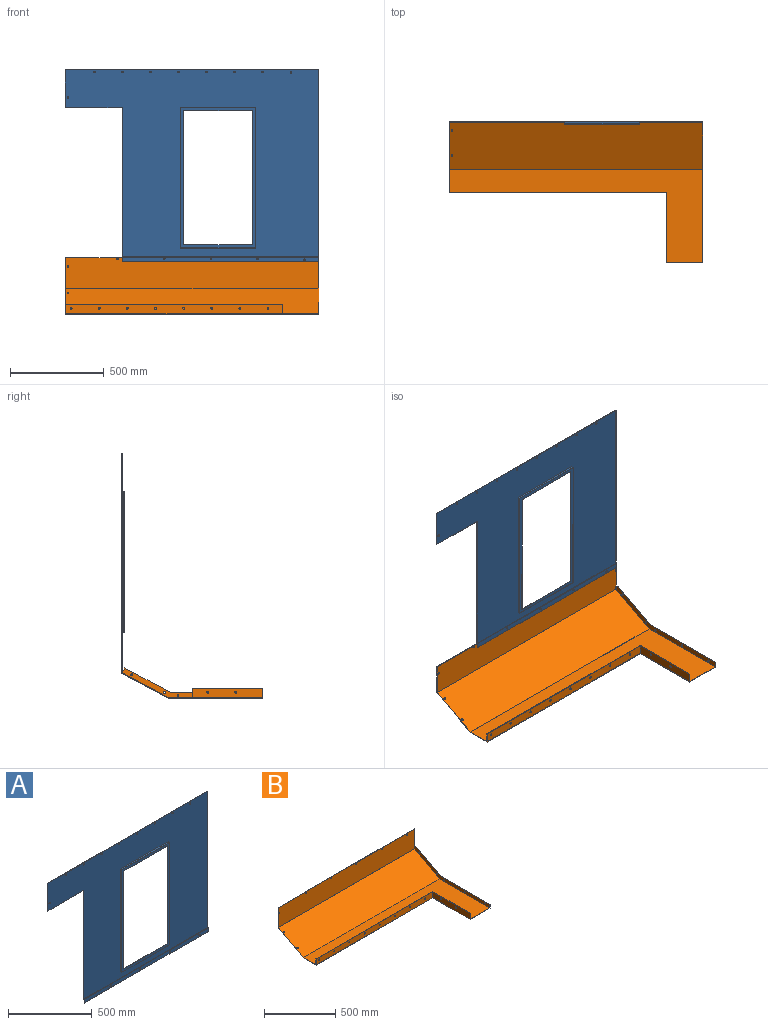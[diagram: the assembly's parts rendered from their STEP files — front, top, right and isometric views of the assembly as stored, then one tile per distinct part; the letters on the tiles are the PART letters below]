
ASSEMBLY  parts=2 mates=1
PART A: 66 faces, bbox 1352x14x1025.5 mm
  f0: plane 368x2mm, normal (0,0,-1), area 736mm2, adj f1,f2,f3,f4
  f1: plane 747.9x400mm, normal (0,1,0), area 35708.8mm2, adj f0,f2,f4,f5,f6,f7,f8,f9
  f2: plane 715.9x2mm, normal (-1,0,0), area 1431.8mm2, adj f0,f1,f3,f9
  f3: plane 751.9x404mm, normal (0,-1,0), area 40316.4mm2, adj f0,f2,f4,f9,f10,f11,f12,f13
  f4: plane 715.9x2mm, normal (1,0,0), area 1431.8mm2, adj f0,f1,f3,f9
  f5: plane 747.9x12mm, normal (-1,0,0), area 8974.8mm2, adj f1,f6,f8,f56
  f6: plane 400x12mm, normal (0,0,-1), area 4800mm2, adj f1,f5,f7,f56
  f7: plane 747.9x12mm, normal (1,0,0), area 8974.8mm2, adj f1,f6,f8,f56
  f8: plane 400x12mm, normal (0,0,1), area 4800mm2, adj f1,f5,f7,f56
  f9: plane 368x2mm, normal (0,0,1), area 736mm2, adj f1,f2,f3,f4
  f10: plane 751.9x12mm, normal (1,0,0), area 9022.8mm2, adj f3,f11,f13,f14
  f11: plane 404x12mm, normal (0,0,1), area 4848mm2, adj f3,f10,f12,f14
  f12: plane 751.9x12mm, normal (-1,0,0), area 9022.8mm2, adj f3,f11,f13,f14
  f13: plane 404x12mm, normal (0,0,-1), area 4848mm2, adj f3,f10,f12,f14
  f14: plane 1352x998.5mm, normal (0,-1,0), area 803361.6mm2, adj f10,f11,f12,f13,f15,f16,f17,f18
  f15: plane 1352x2mm, normal (0,0,1), area 2704mm2, adj f14,f16,f56,f57
  f16: plane 202x2mm, normal (-1,0,0), area 404mm2, adj f14,f15,f17,f56
  f17: plane 304x2mm, normal (0,0,-1), area 608mm2, adj f14,f16,f56,f58
  f18: cylinder r=5mm len=5mm, axis (0,1,0), area 15.7mm2, adj f14,f19,f21,f56
  f19: cylinder r=5mm len=5mm, axis (0,1,0), area 15.7mm2, adj f14,f18,f20,f56
  f20: cylinder r=5mm len=5mm, axis (0,1,0), area 15.7mm2, adj f14,f19,f21,f56
  f21: cylinder r=5mm len=5mm, axis (0,1,0), area 15.7mm2, adj f14,f18,f20,f56
  f22: cylinder r=5mm len=5mm, axis (0,1,0), area 15.7mm2, adj f14,f23,f25,f56
  f23: cylinder r=5mm len=5mm, axis (0,1,0), area 15.7mm2, adj f14,f22,f24,f56
  f24: cylinder r=5mm len=5mm, axis (0,1,0), area 15.7mm2, adj f14,f23,f25,f56
  f25: cylinder r=5mm len=5mm, axis (0,1,0), area 15.7mm2, adj f14,f22,f24,f56
  f26: cylinder r=5mm len=5mm, axis (0,1,0), area 15.7mm2, adj f14,f27,f29,f56
  f27: cylinder r=5mm len=5mm, axis (0,1,0), area 15.7mm2, adj f14,f26,f28,f56
  f28: cylinder r=5mm len=5mm, axis (0,1,0), area 15.7mm2, adj f14,f27,f29,f56
  f29: cylinder r=5mm len=5mm, axis (0,1,0), area 15.7mm2, adj f14,f26,f28,f56
  f30: cylinder r=5mm len=5mm, axis (0,1,0), area 15.7mm2, adj f14,f31,f33,f56
  f31: cylinder r=5mm len=5mm, axis (0,1,0), area 15.7mm2, adj f14,f30,f32,f56
  f32: cylinder r=5mm len=5mm, axis (0,1,0), area 15.7mm2, adj f14,f31,f33,f56
  f33: cylinder r=5mm len=5mm, axis (0,1,0), area 15.7mm2, adj f14,f30,f32,f56
  f34: cylinder r=5mm len=5mm, axis (0,1,0), area 15.7mm2, adj f14,f35,f37,f56
  f35: cylinder r=5mm len=5mm, axis (0,1,0), area 15.7mm2, adj f14,f34,f36,f56
  f36: cylinder r=5mm len=5mm, axis (0,1,0), area 15.7mm2, adj f14,f35,f37,f56
  f37: cylinder r=5mm len=5mm, axis (0,1,0), area 15.7mm2, adj f14,f34,f36,f56
  f38: cylinder r=5mm len=5mm, axis (0,1,0), area 15.7mm2, adj f14,f39,f41,f56
  f39: cylinder r=5mm len=5mm, axis (0,1,0), area 15.7mm2, adj f14,f38,f40,f56
  f40: cylinder r=5mm len=5mm, axis (0,1,0), area 15.7mm2, adj f14,f39,f41,f56
  f41: cylinder r=5mm len=5mm, axis (0,1,0), area 15.7mm2, adj f14,f38,f40,f56
  f42: cylinder r=5mm len=5mm, axis (0,1,0), area 15.7mm2, adj f14,f43,f45,f56
  f43: cylinder r=5mm len=5mm, axis (0,1,0), area 15.7mm2, adj f14,f42,f44,f56
  f44: cylinder r=5mm len=5mm, axis (0,1,0), area 15.7mm2, adj f14,f43,f45,f56
  f45: cylinder r=5mm len=5mm, axis (0,1,0), area 15.7mm2, adj f14,f42,f44,f56
  f46: cylinder r=5mm len=5mm, axis (0,1,0), area 15.7mm2, adj f14,f47,f49,f56
  f47: cylinder r=5mm len=5mm, axis (0,1,0), area 15.7mm2, adj f14,f46,f48,f56
  f48: cylinder r=5mm len=5mm, axis (0,1,0), area 15.7mm2, adj f14,f47,f49,f56
  f49: cylinder r=5mm len=5mm, axis (0,1,0), area 15.7mm2, adj f14,f46,f48,f56
  f50: cylinder r=5mm len=5mm, axis (0,1,0), area 15.7mm2, adj f14,f51,f53,f56
  f51: cylinder r=5mm len=5mm, axis (0,1,0), area 15.7mm2, adj f14,f50,f52,f56
  f52: cylinder r=5mm len=5mm, axis (0,1,0), area 15.7mm2, adj f14,f51,f53,f56
  f53: cylinder r=5mm len=5mm, axis (0,1,0), area 15.7mm2, adj f14,f50,f52,f56
  f54: plane 1048x4mm, normal (0,0,1), area 4192mm2, adj f14,f57,f58,f60
  f55: plane 1048x2mm, normal (0,0,-1), area 2096mm2, adj f57,f58,f60,f61
  f56: plane 1352x1000.5mm, normal (0,1,0), area 810065.2mm2, adj f5,f6,f7,f8,f15,f16,f17,f18
  f57: plane 1025.5x6mm, normal (1,0,0), area 2059mm2, adj f14,f15,f54,f55,f56,f59,f60,f61
  f58: plane 823.5x6mm, normal (-1,0,0), area 1655mm2, adj f14,f17,f54,f55,f56,f59,f60,f61
  f59: plane 1048x4mm, normal (0,0,-1), area 4192mm2, adj f56,f57,f58,f61
  f60: plane 1048x27mm, normal (0,-1,0), area 27981.8mm2, adj f54,f55,f57,f58,f62,f63,f64,f65
  f61: plane 1048x25mm, normal (0,1,0), area 25885.8mm2, adj f55,f57,f58,f59,f62,f63,f64,f65
  f62: cylinder r=5mm len=10mm, axis (0,1,0), area 62.8mm2, adj f60,f61
  f63: cylinder r=5mm len=10mm, axis (0,1,0), area 62.8mm2, adj f60,f61
  f64: cylinder r=5mm len=10mm, axis (0,1,0), area 62.8mm2, adj f60,f61
  f65: cylinder r=5mm len=10mm, axis (0,1,0), area 62.8mm2, adj f60,f61
PART B: 47 faces, bbox 1350x750.5x304 mm
  f0: plane 748.5x159.97mm, normal (-1,0,0), area 22838.6mm2, adj f1,f2,f3,f4,f5,f6,f7,f23
  f1: plane 243.67x129.97mm, normal (0,-0.47,0.88), area 552.3mm2, adj f0,f2,f11,f46
  f2: plane 26.47x14.12mm, normal (0,0.88,0.47), area 60mm2, adj f0,f1,f10,f11
  f3: cylinder r=5mm len=10mm, axis (-1,0,0), area 62.8mm2, adj f0,f11
  f4: cylinder r=5mm len=10mm, axis (-1,0,0), area 62.8mm2, adj f0,f11
  f5: cylinder r=5mm len=10mm, axis (-1,0,0), area 62.8mm2, adj f0,f11
  f6: cylinder r=5mm len=10mm, axis (-1,0,0), area 62.8mm2, adj f0,f11
  f7: cylinder r=5mm len=10mm, axis (-1,0,0), area 62.8mm2, adj f0,f11
  f8: plane 1048x2mm, normal (0,0,1), area 2096mm2, adj f9,f10,f11,f43
  f9: plane 2x1.5mm, normal (-1,0,0), area 3mm2, adj f8,f10,f12,f43
  f10: plane 1350x168.5mm, normal (0,-1,0), area 226550.7mm2, adj f2,f8,f9,f11,f12,f13,f14,f15
  f11: plane 750.5x304mm, normal (1,0,0), area 24742.8mm2, adj f1,f2,f3,f4,f5,f6,f7,f8
  f12: plane 302x2mm, normal (0,0,1), area 604mm2, adj f9,f10,f13,f43
  f13: plane 378.41x302.5mm, normal (-1,0,0), area 1257mm2, adj f10,f12,f23,f26,f27,f29,f32,f43
  f14: cylinder r=5mm len=5mm, axis (0,1,0), area 15.7mm2, adj f10,f15,f17,f43
  f15: cylinder r=5mm len=5mm, axis (0,1,0), area 15.7mm2, adj f10,f14,f16,f43
  f16: cylinder r=5mm len=5mm, axis (0,1,0), area 15.7mm2, adj f10,f15,f17,f43
  f17: cylinder r=5mm len=5mm, axis (0,1,0), area 15.7mm2, adj f10,f14,f16,f43
  f18: cylinder r=5mm len=10mm, axis (0,-1,0), area 62.8mm2, adj f10,f43
  f19: cylinder r=5mm len=10mm, axis (0,-1,0), area 62.8mm2, adj f10,f43
  f20: cylinder r=5mm len=10mm, axis (0,-1,0), area 62.8mm2, adj f10,f43
  f21: cylinder r=5mm len=10mm, axis (0,-1,0), area 62.8mm2, adj f10,f43
  f22: cylinder r=5mm len=10mm, axis (0,-1,0), area 62.8mm2, adj f10,f43
  f23: plane 1348x250.29mm, normal (0,-0.47,0.88), area 382226.4mm2, adj f0,f10,f13,f24,f25,f26
  f24: cylinder r=5mm len=10mm, axis (0,-0.47,0.88), area 62.8mm2, adj f23,f44
  f25: cylinder r=5mm len=10mm, axis (0,-0.47,0.88), area 62.8mm2, adj f23,f44
  f26: plane 1348x498.21mm, normal (0,0,1), area 239040.3mm2, adj f0,f13,f23,f29,f30,f31
  f27: plane 1154.28x52mm, normal (0,-1,0), area 59394.2mm2, adj f13,f28,f32,f33,f34,f35,f36,f37
  f28: plane 372.09x52mm, normal (-1,0,0), area 19191.4mm2, adj f27,f31,f32,f41,f42,f45
  f29: plane 1156.28x50mm, normal (0,1,0), area 57185.7mm2, adj f13,f26,f30,f32,f33,f34,f35,f36
  f30: plane 374.09x50mm, normal (1,0,0), area 18547.2mm2, adj f26,f29,f31,f32,f41,f42
  f31: plane 195.72x52mm, normal (0,-1,0), area 551.4mm2, adj f0,f11,f26,f28,f30,f32,f45,f46
  f32: plane 1156.28x374.09mm, normal (0,0,1), area 3056.7mm2, adj f13,f27,f28,f29,f30,f31
  f33: cylinder r=5mm len=10mm, axis (0,-1,0), area 62.8mm2, adj f27,f29
  f34: cylinder r=5mm len=10mm, axis (0,-1,0), area 62.8mm2, adj f27,f29
  f35: cylinder r=5mm len=10mm, axis (0,-1,0), area 62.8mm2, adj f27,f29
  f36: cylinder r=5mm len=10mm, axis (0,-1,0), area 62.8mm2, adj f27,f29
  f37: cylinder r=5mm len=10mm, axis (0,-1,0), area 62.8mm2, adj f27,f29
  f38: cylinder r=5mm len=10mm, axis (0,-1,0), area 62.8mm2, adj f27,f29
  f39: cylinder r=5mm len=10mm, axis (0,-1,0), area 62.8mm2, adj f27,f29
  f40: cylinder r=5mm len=10mm, axis (0,-1,0), area 62.8mm2, adj f27,f29
  f41: cylinder r=5mm len=10mm, axis (-1,0,0), area 62.8mm2, adj f28,f30
  f42: cylinder r=5mm len=10mm, axis (-1,0,0), area 62.8mm2, adj f28,f30
  f43: plane 1350x169.7mm, normal (0,1,0), area 228170.7mm2, adj f8,f9,f11,f12,f13,f14,f15,f16
  f44: plane 1350x251.79mm, normal (0,0.47,-0.88), area 385088.7mm2, adj f11,f13,f24,f25,f43,f45
  f45: plane 1350x498.71mm, normal (0,0,-1), area 243768.5mm2, adj f11,f13,f27,f28,f31,f44
  f46: plane 490.71x2mm, normal (0,0,1), area 981.4mm2, adj f0,f1,f11,f31
PLACE A t=(389.9,-1551.67,673.74)mm fixed
PLACE B t=(389.9,-1551.67,673.74)mm
MATE fastened B.f18 <-> A.f64  axis (0,-1,0) through (312.9,-52.67,-338.76)mm
